# Revit family: BE_50984.2_de_DE
name_source: partatom
category: Leuchten
units: mm (PartAtom-declared; Revit-internal decimal feet)

## family parameters
Basisbauteil = Fläche
Beim Laden mit Abzugskörper schneiden = Ja
Bemaßung runder Anschluss = Durchmesser verwenden
Gemeinsam genutzt = Nein
Lichtquelle = Nein
Raumberechnungspunkt = Ja
Teiletyp = Normal

## types (1)
- BEGA_50984.2_K3
    Aktualisierung = 2022-05-19T04:00:07
    BEGA_Dummy = Nein
    BEGA_IES = Ja
    BEGA_Intern = Ja
    BEGA_Intern_Konstruktion = Ja
    BEGA_Intern_an = Ja
    BEGA_Intern_aus = Ja
    Beschreibung = Systempendelleuchte
    Beschreibung_Sonderanfertigung = Hier können Sie Informationen zur Sonderanfertigung eintragen.
    Bestellnummer = 50984.2K3
    CE_Konformität = ja
    ENEC = ja
    Energieeffizienzklasse = LED A++ - A
    Farbtemperatur = 3000 K
    Farbwiedergabeindex = CRI > 90
    Gewicht = 0.78 kg
    Hersteller = BEGA
    LED_Modulbezeichnung = LED-1132/930
    Lampe = LED 10.5 W
    Lampenlichtstrom = 1320 lm
    Lastklassifizierung = Beleuchtung
    Lebensdauerkriterien = L70B50 @ 25 °C = 77000 h
    Leuchtenlichtstrom = 481 lm
    Logo = BEGA_Logo.png
    Material_12 = BEGA_Kunststoff_klar
    Material_15 = BEGA_Leuchtmedium_matt
    Material_22 = BEGA_Oberfläche_Aluminium_matt
    Material_35 = BEGA_Oberfläche_Samtschwarz_matt
    Modell = 50984.2K3
    Produktdatenblatt = https://cdn.bega.com
    Scheinlast = 0 VA
    Schutzart = IP 20
    Schutzklasse = III
    Sonderanfertigung = Nein
    Spannung = 240 V
    Strom = 0,35 A
    URL = https://www.bega.com
    Umgebungstemperatur = 25 °C
    Vorgabe-Ansicht = 0 mm  [stored 0 ft]

note: [stored X ft] marks values corroborated as IEEE doubles in the binary element streams (Revit-internal decimal feet)

## geometry (parser evidence)
native form markers: Blend x9
no freeform markers — native parametric forms only
